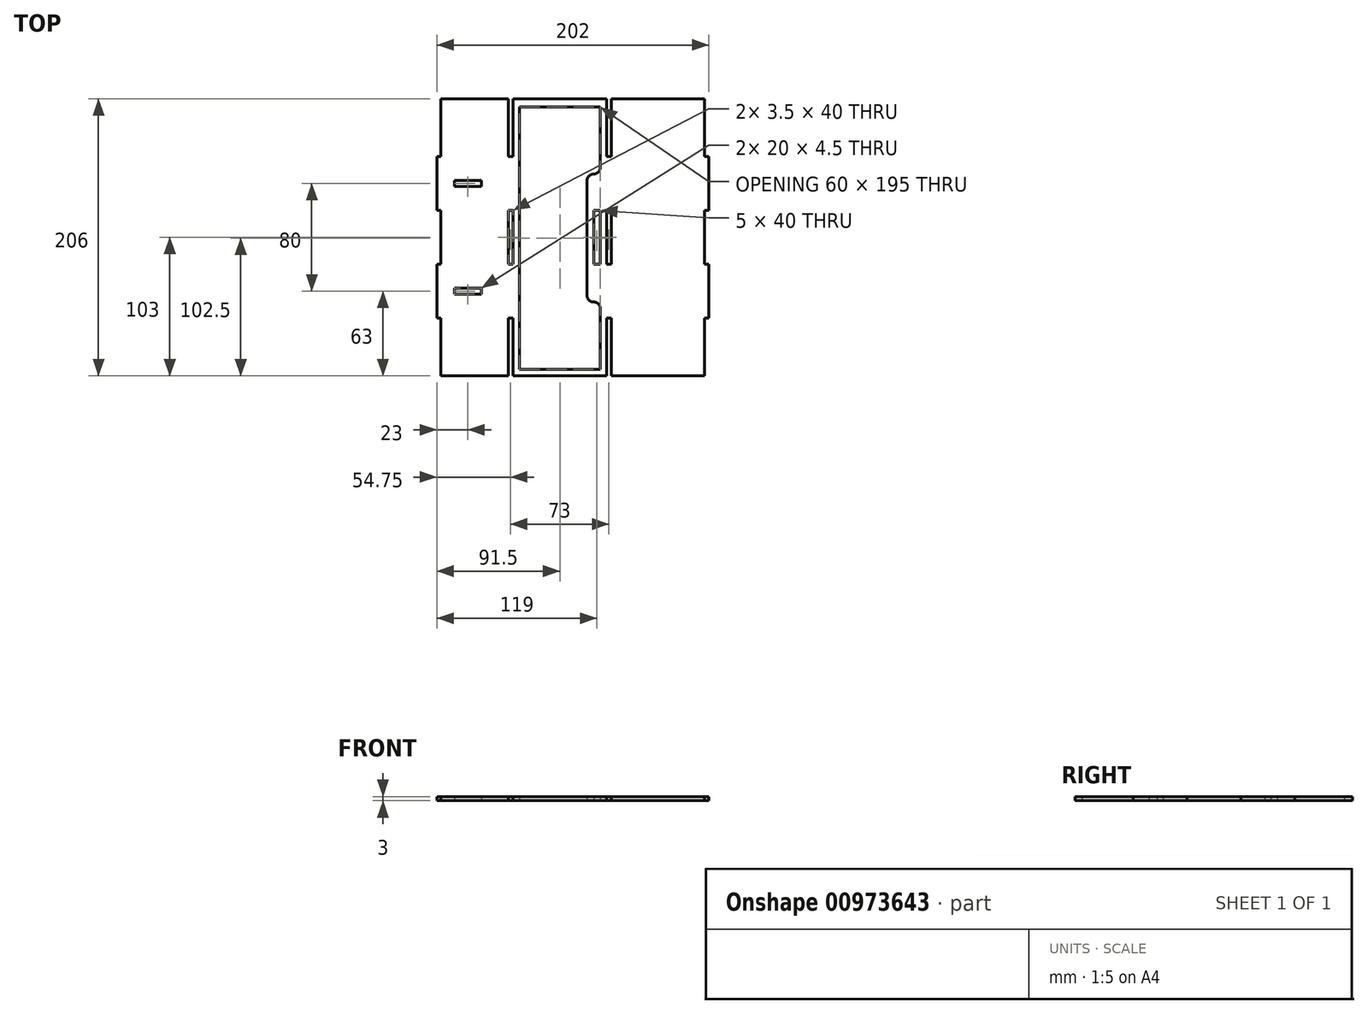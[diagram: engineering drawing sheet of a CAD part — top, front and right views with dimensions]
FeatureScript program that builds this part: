
annotation { "Feature Type Name" : "Feature", "Feature Type Description" : "" }
export const myFeature = defineFeature(function(context is Context, id is Id, definition is map)
    precondition{}
    {
        {
            var Q0;
            Q0=qCreatedBy(makeId("Top.planeOp"),FACE);
            var sketch = newSketch(context, id + "F0", { "sketchPlane" : qUnion([Q0])});
            skLineSegment(sketch, "E0", {"start": v(202, -200) * mm, "end": v(0, -200) * mm});
            skLineSegment(sketch, "E1", {"start": v(0, -200) * mm, "end": v(0, 6) * mm});
            skLineSegment(sketch, "E2", {"start": v(0, 6) * mm, "end": v(202, 6) * mm});
            skLineSegment(sketch, "E3", {"start": v(202, -200) * mm, "end": v(202, 6) * mm});
            skLineSegment(sketch, "E4", {"start": v(0, -200) * mm, "end": v(3, -200) * mm});
            skLineSegment(sketch, "E5", {"start": v(3, -200) * mm, "end": v(3, -157) * mm});
            skLineSegment(sketch, "E6", {"start": v(3, -157) * mm, "end": v(0, -157) * mm});
            skLineSegment(sketch, "E7", {"start": v(0, -157) * mm, "end": v(0, -117) * mm});
            skLineSegment(sketch, "E8", {"start": v(0, -117) * mm, "end": v(3, -117) * mm});
            skLineSegment(sketch, "E9", {"start": v(3, -117) * mm, "end": v(3, -77) * mm});
            skLineSegment(sketch, "E10", {"start": v(3, -77) * mm, "end": v(0, -77) * mm});
            skLineSegment(sketch, "E11", {"start": v(0, -77) * mm, "end": v(0, -37) * mm});
            skLineSegment(sketch, "E12", {"start": v(0, -37) * mm, "end": v(3, -37) * mm});
            skLineSegment(sketch, "E13", {"start": v(3, -37) * mm, "end": v(3, 6) * mm});
            skLineSegment(sketch, "E14", {"start": v(3, -200) * mm, "end": v(53, -200) * mm});
            skLineSegment(sketch, "E15", {"start": v(53, -200) * mm, "end": v(56, -200) * mm});
            skLineSegment(sketch, "E16", {"start": v(53, -157) * mm, "end": v(53, -200) * mm});
            skLineSegment(sketch, "E17", {"start": v(53, -117) * mm, "end": v(53, -77) * mm});
            skLineSegment(sketch, "E18", {"start": v(53, 6) * mm, "end": v(53, -37) * mm});
            skLineSegment(sketch, "E19", {"start": v(56, -200) * mm, "end": v(126, -200) * mm});
            skLineSegment(sketch, "E20", {"start": v(126, -200) * mm, "end": v(126, -157) * mm});
            skLineSegment(sketch, "E21", {"start": v(126, -117) * mm, "end": v(126, -77) * mm});
            skLineSegment(sketch, "E22", {"start": v(126, -37) * mm, "end": v(126, 6) * mm});
            skLineSegment(sketch, "E23", {"start": v(202, -200) * mm, "end": v(199, -200) * mm});
            skLineSegment(sketch, "E24", {"start": v(199, -200) * mm, "end": v(199, -157) * mm});
            skLineSegment(sketch, "E25", {"start": v(199, -157) * mm, "end": v(202, -157) * mm});
            skLineSegment(sketch, "E26", {"start": v(199, -117) * mm, "end": v(199, -77) * mm});
            skLineSegment(sketch, "E27", {"start": v(199, -77) * mm, "end": v(202, -77) * mm});
            skLineSegment(sketch, "E28", {"start": v(199, -117) * mm, "end": v(202, -117) * mm});
            skLineSegment(sketch, "E29", {"start": v(199, -37) * mm, "end": v(199, 6) * mm});
            skLineSegment(sketch, "E30", {"start": v(199, -37) * mm, "end": v(202, -37) * mm});
            skLineSegment(sketch, "E31", {"start": v(53, -157) * mm, "end": v(56.5, -157) * mm});
            skLineSegment(sketch, "E32", {"start": v(56.5, -157) * mm, "end": v(56.5, -200) * mm});
            skLineSegment(sketch, "E33", {"start": v(53, -117) * mm, "end": v(56.5, -117) * mm});
            skLineSegment(sketch, "E34", {"start": v(56.5, -117) * mm, "end": v(56.5, -77) * mm});
            skLineSegment(sketch, "E35", {"start": v(56.5, -77) * mm, "end": v(53, -77) * mm});
            skLineSegment(sketch, "E36", {"start": v(56.5, -37) * mm, "end": v(56.5, 6) * mm});
            skLineSegment(sketch, "E37", {"start": v(53, -37) * mm, "end": v(56.5, -37) * mm});
            skLineSegment(sketch, "E38", {"start": v(126, -157) * mm, "end": v(129.5, -157) * mm});
            skLineSegment(sketch, "E39", {"start": v(129.5, -157) * mm, "end": v(129.5, -200) * mm});
            skLineSegment(sketch, "E40", {"start": v(126, -117) * mm, "end": v(129.5, -117) * mm});
            skLineSegment(sketch, "E41", {"start": v(129.5, -117) * mm, "end": v(129.5, -77) * mm});
            skLineSegment(sketch, "E42", {"start": v(129.5, -77) * mm, "end": v(126, -77) * mm});
            skLineSegment(sketch, "E43", {"start": v(129.5, -37) * mm, "end": v(129.5, 6) * mm});
            skLineSegment(sketch, "E44", {"start": v(126, -37) * mm, "end": v(129.5, -37) * mm});
            skLineSegment(sketch, "E45", {"start": v(61.5, -97) * mm, "end": v(61.5, 0) * mm});
            skLineSegment(sketch, "E46", {"start": v(61.5, 0) * mm, "end": v(121.5, 0) * mm});
            skLineSegment(sketch, "E47", {"start": v(121.5, -195) * mm, "end": v(61.5, -195) * mm});
            skLineSegment(sketch, "E48", {"start": v(61.5, -195) * mm, "end": v(61.5, -97) * mm});
            skLineSegment(sketch, "E49", {"start": v(121.5, -195) * mm, "end": v(121.5, -145) * mm});
            skLineSegment(sketch, "E50", {"start": v(121.5, 0) * mm, "end": v(121.5, -50) * mm});
            skLineSegment(sketch, "E51", {"start": v(111.5, -145) * mm, "end": v(121.5, -145) * mm});
            skLineSegment(sketch, "E52", {"start": v(111.5, -50) * mm, "end": v(121.5, -50) * mm});
            skLineSegment(sketch, "E53", {"start": v(111.5, -145) * mm, "end": v(111.5, -50) * mm});
            skLineSegment(sketch, "E54", {"start": v(121.5, -117) * mm, "end": v(121.5, -77) * mm});
            skLineSegment(sketch, "E55", {"start": v(121.5, -77) * mm, "end": v(116.5, -77) * mm});
            skLineSegment(sketch, "E56", {"start": v(116.5, -77) * mm, "end": v(116.5, -117) * mm});
            skLineSegment(sketch, "E57", {"start": v(116.5, -117) * mm, "end": v(121.5, -117) * mm});
            skPoint(sketch, "E58.startSnap0", {"position": v(0, -137) * mm});
            skLineSegment(sketch, "E59", {"start": v(33, -137) * mm, "end": v(33, -134.75) * mm});
            skLineSegment(sketch, "E60", {"start": v(33, -134.75) * mm, "end": v(33, -139.25) * mm});
            skLineSegment(sketch, "E61", {"start": v(33, -139.25) * mm, "end": v(13, -139.25) * mm});
            skLineSegment(sketch, "E62", {"start": v(13, -139.25) * mm, "end": v(13, -134.75) * mm});
            skLineSegment(sketch, "E63", {"start": v(13, -134.75) * mm, "end": v(33, -134.75) * mm});
            skLineSegment(sketch, "E64", {"start": v(33, -57) * mm, "end": v(33, -54.75) * mm});
            skPoint(sketch, "E64.startSnap0", {"position": v(0, -57) * mm});
            skLineSegment(sketch, "E65", {"start": v(33, -57) * mm, "end": v(33, -59.25) * mm});
            skLineSegment(sketch, "E66", {"start": v(33, -59.25) * mm, "end": v(13, -59.25) * mm});
            skLineSegment(sketch, "E67", {"start": v(13, -59.25) * mm, "end": v(13, -54.75) * mm});
            skLineSegment(sketch, "E68", {"start": v(13, -54.75) * mm, "end": v(33, -54.75) * mm});
            skSolve(sketch);
        }
        {
            var Q0;
            {var subQ22=sQuery(id+"F0.wireOp",EDGE,"E5");Q0=makeQuery(id+"F0.imprint","IMPRINT",FACE,{"disambiguationData":[TD([[makeQuery(id+"F0.imprint","IMPRINT",EDGE,{"derivedFrom":subQ22}),-1.0]])]});}
            extrude(context, id + "F1", {"entities" : qUnion([Q0]), "depth" : 3 * mm, "offsetDistance" : 25 * mm});
        }
        {
            var Q0;
            Q0=makeQuery(id+"F1.opExtrude","SWEPT_EDGE",EDGE,{"disambiguationData":[OSD([sQuery(id+"F0.wireOp",EDGE,"E50"),sQuery(id+"F0.wireOp",EDGE,"E52")])]});
            fillet(context, id + "F2", {"entities" : qUnion([Q0]), "radius" : 5 * mm, "tangentPropagation" : true, "allowEdgeOverflow" : false});
        }
        {
            var Q0;
            Q0=makeQuery(id+"F1.opExtrude","SWEPT_EDGE",EDGE,{"disambiguationData":[OSD([sQuery(id+"F0.wireOp",EDGE,"E52"),sQuery(id+"F0.wireOp",EDGE,"E53")])]});
            fillet(context, id + "F3", {"entities" : qUnion([Q0]), "radius" : 5 * mm, "tangentPropagation" : true, "allowEdgeOverflow" : false});
        }
        {
            var Q0;
            Q0=makeQuery(id+"F1.opExtrude","SWEPT_EDGE",EDGE,{"disambiguationData":[OSD([sQuery(id+"F0.wireOp",EDGE,"E49"),sQuery(id+"F0.wireOp",EDGE,"E51")])]});
            var Q1;
            Q1=makeQuery(id+"F1.opExtrude","SWEPT_EDGE",EDGE,{"disambiguationData":[OSD([sQuery(id+"F0.wireOp",EDGE,"E51"),sQuery(id+"F0.wireOp",EDGE,"E53")])]});
            fillet(context, id + "F4", {"entities" : qUnion([Q0, Q1]), "radius" : 5 * mm, "tangentPropagation" : true, "allowEdgeOverflow" : false});
        }
    });
